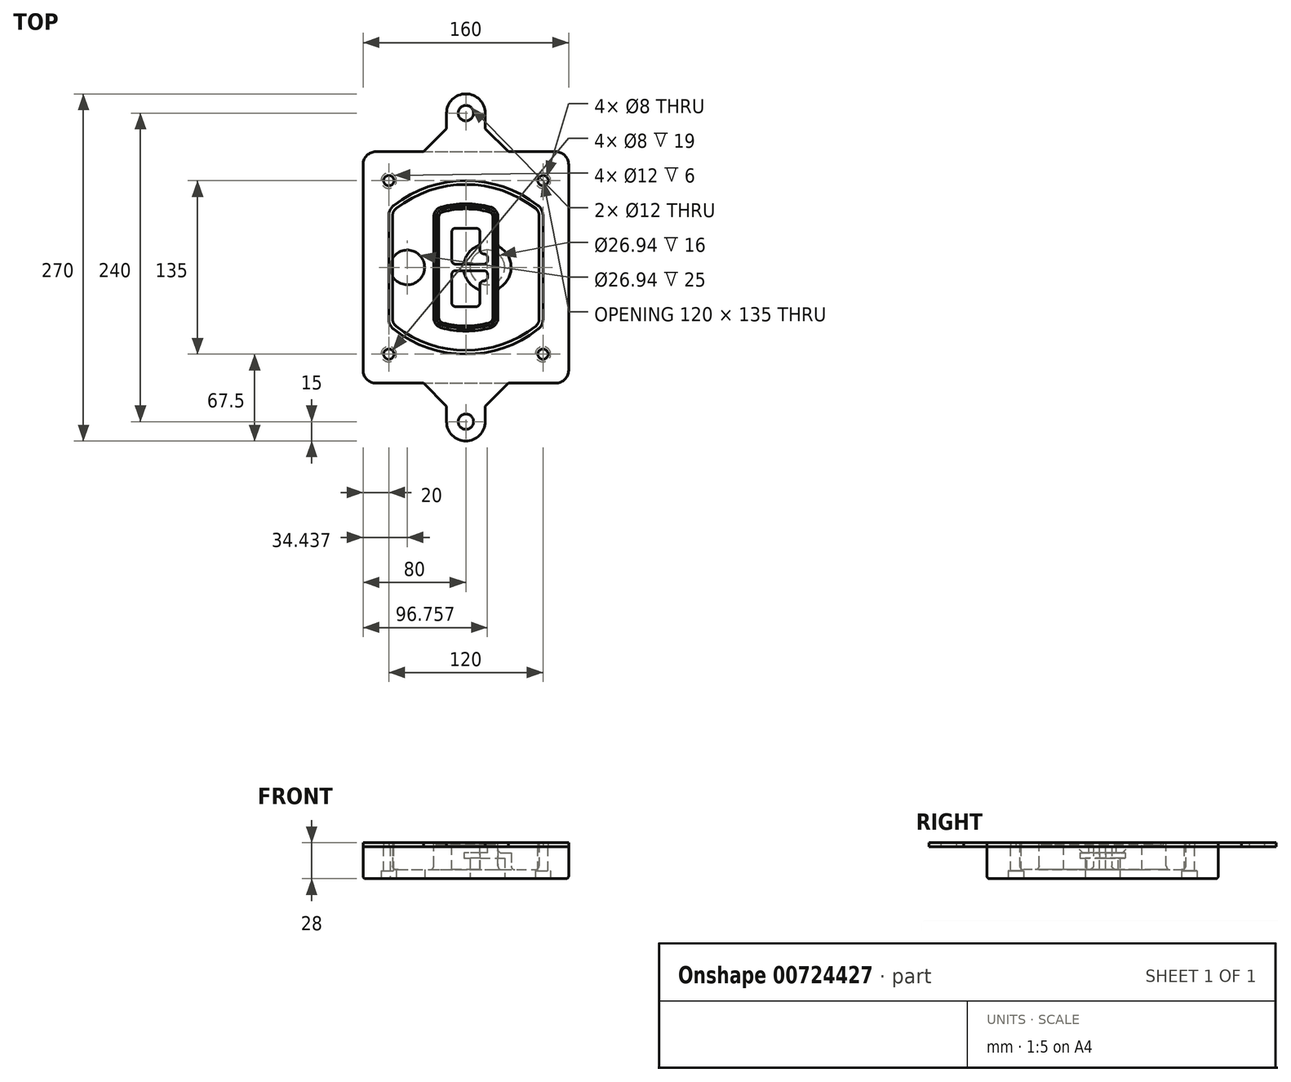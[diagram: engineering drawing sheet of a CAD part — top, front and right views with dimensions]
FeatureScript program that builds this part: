
annotation { "Feature Type Name" : "Feature", "Feature Type Description" : "" }
export const myFeature = defineFeature(function(context is Context, id is Id, definition is map)
    precondition{}
    {
        {
            var Q0;
            Q0=qCreatedBy(makeId("Top.planeOp"),FACE);
            var sketch = newSketch(context, id + "F0", { "sketchPlane" : qUnion([Q0])});
            skPoint(sketch, "E0.rect.middle", {"position": v(0, 0) * mm});
            skLineSegment(sketch, "E1.bottom", {"start": v(-70, -90) * mm, "end": v(70, -90) * mm});
            skLineSegment(sketch, "E1.top", {"start": v(-70, 90) * mm, "end": v(70, 90) * mm});
            skLineSegment(sketch, "E1.left", {"start": v(-80, -80) * mm, "end": v(-80, 80) * mm});
            skLineSegment(sketch, "E1.right", {"start": v(80, -80) * mm, "end": v(80, 80) * mm});
            skLineSegment(sketch, "E2", {"start": v(-80, 90) * mm, "end": v(80, -90) * mm, "construction": true});
            skLineSegment(sketch, "E3", {"start": v(80, 90) * mm, "end": v(-80, -90) * mm, "construction": true});
            skCircle(sketch, "E4", {"center": v(-60, 67.5) * mm, "radius": 4 * mm});
            skCircle(sketch, "E5", {"center": v(60, 67.5) * mm, "radius": 4 * mm});
            skCircle(sketch, "E6", {"center": v(60, -67.5) * mm, "radius": 4 * mm});
            skCircle(sketch, "E7", {"center": v(-60, -67.5) * mm, "radius": 4 * mm});
            skLineSegment(sketch, "E8", {"start": v(-60, 67.5) * mm, "end": v(60, 67.5) * mm, "construction": true});
            skLineSegment(sketch, "E9", {"start": v(60, 67.5) * mm, "end": v(60, -67.5) * mm, "construction": true});
            skLineSegment(sketch, "E10", {"start": v(60, -67.5) * mm, "end": v(-60, -67.5) * mm, "construction": true});
            skLineSegment(sketch, "E11", {"start": v(-60, -67.5) * mm, "end": v(-60, 67.5) * mm, "construction": true});
            skLineSegment(sketch, "E12", {"start": v(-60, 40.3) * mm, "end": v(-60, -40.3) * mm});
            skLineSegment(sketch, "E13", {"start": v(60, 40.3) * mm, "end": v(60, -40.3) * mm});
            skArc(sketch, "E14", {"start": v(56.15, 48.18) * mm, "mid": v(0, 67.5) * mm, "end": v(-56.15, 48.18) * mm});
            skArc(sketch, "E15", {"start": v(-56.15, -48.18) * mm, "mid": v(0, -67.5) * mm, "end": v(56.15, -48.18) * mm});
            skLineSegment(sketch, "E16", {"start": v(-60, 0) * mm, "end": v(60, 0) * mm, "construction": true});
            skPoint(sketch, "E17.visualSharp", {"position": v(-60, -45) * mm});
            skArc(sketch, "E17.filletArc", {"start": v(-60, -40.3) * mm, "mid": v(-58.99, -44.68) * mm, "end": v(-56.15, -48.18) * mm});
            skPoint(sketch, "E18.visualSharp", {"position": v(-60, 45) * mm});
            skArc(sketch, "E18.filletArc", {"start": v(-56.15, 48.18) * mm, "mid": v(-58.99, 44.68) * mm, "end": v(-60, 40.3) * mm});
            skPoint(sketch, "E19.visualSharp", {"position": v(60, 45) * mm});
            skArc(sketch, "E19.filletArc", {"start": v(60, 40.3) * mm, "mid": v(58.99, 44.68) * mm, "end": v(56.15, 48.18) * mm});
            skPoint(sketch, "E20.visualSharp", {"position": v(60, -45) * mm});
            skArc(sketch, "E20.filletArc", {"start": v(56.15, -48.18) * mm, "mid": v(58.99, -44.68) * mm, "end": v(60, -40.3) * mm});
            skPoint(sketch, "E21.visualSharp", {"position": v(-80, 90) * mm});
            skArc(sketch, "E21.filletArc", {"start": v(-70, 90) * mm, "mid": v(-77.07, 87.07) * mm, "end": v(-80, 80) * mm});
            skPoint(sketch, "E22.visualSharp", {"position": v(80, 90) * mm});
            skArc(sketch, "E22.filletArc", {"start": v(80, 80) * mm, "mid": v(77.07, 87.07) * mm, "end": v(70, 90) * mm});
            skPoint(sketch, "E23.visualSharp", {"position": v(80, -90) * mm});
            skArc(sketch, "E23.filletArc", {"start": v(70, -90) * mm, "mid": v(77.07, -87.07) * mm, "end": v(80, -80) * mm});
            skPoint(sketch, "E24.visualSharp", {"position": v(-80, -90) * mm});
            skArc(sketch, "E24.filletArc", {"start": v(-80, -80) * mm, "mid": v(-77.07, -87.07) * mm, "end": v(-70, -90) * mm});
            skArc(sketch, "E25.0", {"start": v(57, 40.3) * mm, "mid": v(56.3, 43.36) * mm, "end": v(54.3, 45.81) * mm});
            skLineSegment(sketch, "E25.1", {"start": v(57, 40.3) * mm, "end": v(57, -40.3) * mm});
            skArc(sketch, "E25.2", {"start": v(54.3, -45.81) * mm, "mid": v(56.3, -43.36) * mm, "end": v(57, -40.3) * mm});
            skArc(sketch, "E25.3", {"start": v(-54.3, -45.81) * mm, "mid": v(0, -64.5) * mm, "end": v(54.3, -45.81) * mm});
            skArc(sketch, "E25.4", {"start": v(-57, -40.3) * mm, "mid": v(-56.3, -43.36) * mm, "end": v(-54.3, -45.81) * mm});
            skArc(sketch, "E25.5", {"start": v(54.3, 45.81) * mm, "mid": v(0, 64.5) * mm, "end": v(-54.3, 45.81) * mm});
            skLineSegment(sketch, "E25.6", {"start": v(-57, 40.3) * mm, "end": v(-57, -40.3) * mm});
            skArc(sketch, "E25.7", {"start": v(-54.3, 45.81) * mm, "mid": v(-56.3, 43.36) * mm, "end": v(-57, 40.3) * mm});
            skArc(sketch, "E26.0", {"start": v(-58.62, 51.33) * mm, "mid": v(-62.58, 46.43) * mm, "end": v(-64, 40.3) * mm});
            skArc(sketch, "E26.1", {"start": v(58.62, 51.33) * mm, "mid": v(0, 71.5) * mm, "end": v(-58.62, 51.33) * mm});
            skArc(sketch, "E26.2", {"start": v(64, 40.3) * mm, "mid": v(62.58, 46.43) * mm, "end": v(58.62, 51.33) * mm});
            skLineSegment(sketch, "E26.3", {"start": v(64, 40.3) * mm, "end": v(64, -40.3) * mm});
            skArc(sketch, "E26.4", {"start": v(58.62, -51.33) * mm, "mid": v(62.58, -46.43) * mm, "end": v(64, -40.3) * mm});
            skLineSegment(sketch, "E26.5", {"start": v(-64, 40.3) * mm, "end": v(-64, -40.3) * mm});
            skArc(sketch, "E26.6", {"start": v(-58.62, -51.33) * mm, "mid": v(0, -71.5) * mm, "end": v(58.62, -51.33) * mm});
            skArc(sketch, "E26.7", {"start": v(-64, -40.3) * mm, "mid": v(-62.58, -46.43) * mm, "end": v(-58.62, -51.33) * mm});
            skSolve(sketch);
        }
        {
            var Q0;
            Q0=makeQuery(id+"F0.imprint","IMPRINT",FACE,{"disambiguationData":[TD([[makeQuery(id+"F0.imprint","IMPRINT",EDGE,{"derivedFrom":sQuery(id+"F0.wireOp",EDGE,"E1.bottom")}),1.0]])]});
            var Q1;
            Q1=makeQuery(id+"F0.imprint","IMPRINT",FACE,{"disambiguationData":[TD([[makeQuery(id+"F0.imprint","IMPRINT",EDGE,{"derivedFrom":sQuery(id+"F0.wireOp",EDGE,"E12")}),1.0]])]});
            var Q2;
            Q2=makeQuery(id+"F0.imprint","IMPRINT",FACE,{"disambiguationData":[TD([[makeQuery(id+"F0.imprint","IMPRINT",EDGE,{"derivedFrom":sQuery(id+"F0.wireOp",EDGE,"E25.0")}),1.0]])]});
            var Q3;
            Q3=makeQuery(id+"F0.imprint","IMPRINT",FACE,{"disambiguationData":[TD([[makeQuery(id+"F0.imprint","IMPRINT",EDGE,{"derivedFrom":sQuery(id+"F0.wireOp",EDGE,"E12")}),-1.0]])]});
            extrude(context, id + "F1", {"entities" : qUnion([Q0, Q1, Q2, Q3]), "oppositeDirection" : true, "depth" : 25 * mm});
        }
        {
            var Q0;
            Q0=makeQuery(id+"F0.imprint","IMPRINT",FACE,{"disambiguationData":[TD([[makeQuery(id+"F0.imprint","IMPRINT",EDGE,{"derivedFrom":sQuery(id+"F0.wireOp",EDGE,"E12")}),1.0]])]});
            extrude(context, id + "F2", {"entities" : qUnion([Q0]), "operationType" : NewBodyOperationType.ADD, "depth" : 3 * mm});
        }
        {
            var Q0;
            Q0=makeQuery(id+"F0.imprint","IMPRINT",FACE,{"disambiguationData":[TD([[makeQuery(id+"F0.imprint","IMPRINT",EDGE,{"derivedFrom":sQuery(id+"F0.wireOp",EDGE,"E25.0")}),1.0]])]});
            extrude(context, id + "F3", {"entities" : qUnion([Q0]), "operationType" : NewBodyOperationType.REMOVE, "oppositeDirection" : true, "depth" : 18 * mm});
        }
        {
            var Q0;
            Q0=makeQuery(id+"F2.opExtrude","CAP_FACE",FACE,{"disambiguationData":[OSD([sQuery(id+"F0.wireOp",EDGE,"E12"),sQuery(id+"F0.wireOp",EDGE,"E13"),sQuery(id+"F0.wireOp",EDGE,"E14"),sQuery(id+"F0.wireOp",EDGE,"E15"),sQuery(id+"F0.wireOp",EDGE,"E17.filletArc"),sQuery(id+"F0.wireOp",EDGE,"E18.filletArc"),sQuery(id+"F0.wireOp",EDGE,"E19.filletArc"),sQuery(id+"F0.wireOp",EDGE,"E20.filletArc"),sQuery(id+"F0.wireOp",EDGE,"E25.0"),sQuery(id+"F0.wireOp",EDGE,"E25.1"),sQuery(id+"F0.wireOp",EDGE,"E25.2"),sQuery(id+"F0.wireOp",EDGE,"E25.3"),sQuery(id+"F0.wireOp",EDGE,"E25.4"),sQuery(id+"F0.wireOp",EDGE,"E25.5"),sQuery(id+"F0.wireOp",EDGE,"E25.6"),sQuery(id+"F0.wireOp",EDGE,"E25.7")])],"isStart":false});
            var sketch = newSketch(context, id + "F4", { "sketchPlane" : qUnion([Q0])});
            skArc(sketch, "E27.0", {"start": v(-19.08, -46.97) * mm, "mid": v(0, -49.5) * mm, "end": v(19.08, -46.97) * mm});
            skArc(sketch, "E28.0", {"start": v(19.08, 46.97) * mm, "mid": v(0, 49.5) * mm, "end": v(-19.08, 46.97) * mm});
            skLineSegment(sketch, "E29", {"start": v(-25, 39.25) * mm, "end": v(-25, -39.25) * mm});
            skLineSegment(sketch, "E30", {"start": v(25, 39.25) * mm, "end": v(25, -39.25) * mm});
            skLineSegment(sketch, "E31", {"start": v(-25, 45.1) * mm, "end": v(25, 45.1) * mm, "construction": true});
            skLineSegment(sketch, "E32", {"start": v(-25, -45.1) * mm, "end": v(25, -45.1) * mm, "construction": true});
            skPoint(sketch, "E33.visualSharp", {"position": v(-25, 45.1) * mm});
            skArc(sketch, "E33.filletArc", {"start": v(-19.08, 46.97) * mm, "mid": v(-23.35, 44.11) * mm, "end": v(-25, 39.25) * mm});
            skPoint(sketch, "E34.visualSharp", {"position": v(25, 45.1) * mm});
            skArc(sketch, "E34.filletArc", {"start": v(25, 39.25) * mm, "mid": v(23.35, 44.11) * mm, "end": v(19.08, 46.97) * mm});
            skPoint(sketch, "E35.visualSharp", {"position": v(25, -45.1) * mm});
            skArc(sketch, "E35.filletArc", {"start": v(19.08, -46.97) * mm, "mid": v(23.35, -44.11) * mm, "end": v(25, -39.25) * mm});
            skPoint(sketch, "E36.visualSharp", {"position": v(-25, -45.1) * mm});
            skArc(sketch, "E36.filletArc", {"start": v(-25, -39.25) * mm, "mid": v(-23.35, -44.11) * mm, "end": v(-19.08, -46.97) * mm});
            skArc(sketch, "E37.0", {"start": v(54.3, 45.81) * mm, "mid": v(0, 64.5) * mm, "end": v(-54.3, 45.81) * mm});
            skArc(sketch, "E37.1", {"start": v(-54.3, 45.81) * mm, "mid": v(-56.3, 43.36) * mm, "end": v(-57, 40.3) * mm});
            skLineSegment(sketch, "E37.2", {"start": v(-57, 40.3) * mm, "end": v(-57, -40.3) * mm});
            skArc(sketch, "E37.3", {"start": v(-57, -40.3) * mm, "mid": v(-56.3, -43.36) * mm, "end": v(-54.3, -45.81) * mm});
            skArc(sketch, "E37.4", {"start": v(-54.3, -45.81) * mm, "mid": v(0, -64.5) * mm, "end": v(54.3, -45.81) * mm});
            skArc(sketch, "E37.5", {"start": v(54.3, -45.81) * mm, "mid": v(56.3, -43.36) * mm, "end": v(57, -40.3) * mm});
            skLineSegment(sketch, "E37.6", {"start": v(57, 40.3) * mm, "end": v(57, -40.3) * mm});
            skArc(sketch, "E37.7", {"start": v(57, 40.3) * mm, "mid": v(56.3, 43.36) * mm, "end": v(54.3, 45.81) * mm});
            skLineSegment(sketch, "E38.0", {"start": v(23, 39.25) * mm, "end": v(23, -39.25) * mm});
            skArc(sketch, "E38.1", {"start": v(18.56, -45.04) * mm, "mid": v(21.76, -42.9) * mm, "end": v(23, -39.25) * mm});
            skArc(sketch, "E38.2", {"start": v(-18.56, -45.04) * mm, "mid": v(0, -47.5) * mm, "end": v(18.56, -45.04) * mm});
            skArc(sketch, "E38.3", {"start": v(-23, -39.25) * mm, "mid": v(-21.76, -42.9) * mm, "end": v(-18.56, -45.04) * mm});
            skLineSegment(sketch, "E38.4", {"start": v(-23, 39.25) * mm, "end": v(-23, -39.25) * mm});
            skArc(sketch, "E38.5", {"start": v(23, 39.25) * mm, "mid": v(21.76, 42.9) * mm, "end": v(18.56, 45.04) * mm});
            skArc(sketch, "E38.6", {"start": v(-18.56, 45.04) * mm, "mid": v(-21.76, 42.9) * mm, "end": v(-23, 39.25) * mm});
            skArc(sketch, "E38.7", {"start": v(18.56, 45.04) * mm, "mid": v(0, 47.5) * mm, "end": v(-18.56, 45.04) * mm});
            skArc(sketch, "E39.0", {"start": v(21, 39.25) * mm, "mid": v(20.18, 41.68) * mm, "end": v(18.04, 43.1) * mm});
            skLineSegment(sketch, "E39.1", {"start": v(21, 39.25) * mm, "end": v(21, -39.25) * mm});
            skArc(sketch, "E39.2", {"start": v(18.04, -43.1) * mm, "mid": v(20.18, -41.68) * mm, "end": v(21, -39.25) * mm});
            skArc(sketch, "E39.3", {"start": v(-18.04, -43.1) * mm, "mid": v(0, -45.5) * mm, "end": v(18.04, -43.1) * mm});
            skArc(sketch, "E39.4", {"start": v(-21, -39.25) * mm, "mid": v(-20.18, -41.68) * mm, "end": v(-18.04, -43.1) * mm});
            skArc(sketch, "E39.5", {"start": v(18.04, 43.1) * mm, "mid": v(0, 45.5) * mm, "end": v(-18.04, 43.1) * mm});
            skLineSegment(sketch, "E39.6", {"start": v(-21, 39.25) * mm, "end": v(-21, -39.25) * mm});
            skArc(sketch, "E39.7", {"start": v(-18.04, 43.1) * mm, "mid": v(-20.18, 41.68) * mm, "end": v(-21, 39.25) * mm});
            skLineSegment(sketch, "E40", {"start": v(-25, 0) * mm, "end": v(25, 0) * mm, "construction": true});
            skLineSegment(sketch, "E41", {"start": v(-11, 5.5) * mm, "end": v(-11, 27.5) * mm});
            skLineSegment(sketch, "E42", {"start": v(-8, 30.5) * mm, "end": v(8, 30.5) * mm});
            skLineSegment(sketch, "E43", {"start": v(11, 27.5) * mm, "end": v(11, 13.5) * mm});
            skLineSegment(sketch, "E44", {"start": v(14, 10.5) * mm, "end": v(14, 10.5) * mm});
            skLineSegment(sketch, "E45", {"start": v(17, 7.5) * mm, "end": v(17, 5.5) * mm});
            skLineSegment(sketch, "E46", {"start": v(14, 2.5) * mm, "end": v(-8, 2.5) * mm});
            skPoint(sketch, "E47.visualSharp", {"position": v(-11, 30.5) * mm});
            skArc(sketch, "E47.filletArc", {"start": v(-8, 30.5) * mm, "mid": v(-10.12, 29.62) * mm, "end": v(-11, 27.5) * mm});
            skPoint(sketch, "E48.visualSharp", {"position": v(11, 30.5) * mm});
            skArc(sketch, "E48.filletArc", {"start": v(11, 27.5) * mm, "mid": v(10.12, 29.62) * mm, "end": v(8, 30.5) * mm});
            skPoint(sketch, "E49.visualSharp", {"position": v(11, 10.5) * mm});
            skArc(sketch, "E49.filletArc", {"start": v(11, 13.5) * mm, "mid": v(11.88, 11.38) * mm, "end": v(14, 10.5) * mm});
            skPoint(sketch, "E50.visualSharp", {"position": v(17, 10.5) * mm});
            skArc(sketch, "E50.filletArc", {"start": v(17, 7.5) * mm, "mid": v(16.12, 9.62) * mm, "end": v(14, 10.5) * mm});
            skPoint(sketch, "E51.visualSharp", {"position": v(17, 2.5) * mm});
            skArc(sketch, "E51.filletArc", {"start": v(14, 2.5) * mm, "mid": v(16.12, 3.38) * mm, "end": v(17, 5.5) * mm});
            skPoint(sketch, "E52.visualSharp", {"position": v(-11, 2.5) * mm});
            skArc(sketch, "E52.filletArc", {"start": v(-11, 5.5) * mm, "mid": v(-10.12, 3.38) * mm, "end": v(-8, 2.5) * mm});
            skLineSegment(sketch, "E53.0.MirrorCS", {"start": v(14, -2.5) * mm, "end": v(-8, -2.5) * mm});
            skArc(sketch, "E54.0.MirrorCS", {"start": v(-11, -5.5) * mm, "mid": v(-10.12, -3.38) * mm, "end": v(-8, -2.5) * mm});
            skLineSegment(sketch, "E55.0.MirrorCS", {"start": v(-11, -5.5) * mm, "end": v(-11, -27.5) * mm});
            skArc(sketch, "E56.0.MirrorCS", {"start": v(-8, -30.5) * mm, "mid": v(-10.12, -29.62) * mm, "end": v(-11, -27.5) * mm});
            skLineSegment(sketch, "E57.0.MirrorCS", {"start": v(-8, -30.5) * mm, "end": v(8, -30.5) * mm});
            skArc(sketch, "E58.0.MirrorCS", {"start": v(11, -27.5) * mm, "mid": v(10.12, -29.62) * mm, "end": v(8, -30.5) * mm});
            skLineSegment(sketch, "E59.0.MirrorCS", {"start": v(11, -27.5) * mm, "end": v(11, -13.5) * mm});
            skArc(sketch, "E60.0.MirrorCS", {"start": v(11, -13.5) * mm, "mid": v(11.88, -11.38) * mm, "end": v(14, -10.5) * mm});
            skArc(sketch, "E61.0.MirrorCS", {"start": v(17, -7.5) * mm, "mid": v(16.12, -9.62) * mm, "end": v(14, -10.5) * mm});
            skLineSegment(sketch, "E62.0.MirrorCS", {"start": v(17, -7.5) * mm, "end": v(17, -5.5) * mm});
            skArc(sketch, "E63.0.MirrorCS", {"start": v(14, -2.5) * mm, "mid": v(16.12, -3.38) * mm, "end": v(17, -5.5) * mm});
            skSolve(sketch);
        }
        {
            var Q0;
            Q0=makeQuery(id+"F4.imprint","IMPRINT",FACE,{"disambiguationData":[TD([[makeQuery(id+"F4.imprint","IMPRINT",EDGE,{"derivedFrom":sQuery(id+"F4.wireOp",EDGE,"E27.0")}),1.0]])]});
            var Q1;
            Q1=makeQuery(id+"F4.imprint","IMPRINT",FACE,{"disambiguationData":[TD([[makeQuery(id+"F4.imprint","IMPRINT",EDGE,{"derivedFrom":sQuery(id+"F4.wireOp",EDGE,"E38.0")}),-1.0]])]});
            var Q2;
            Q2=makeQuery(id+"F4.imprint","IMPRINT",FACE,{"disambiguationData":[TD([[makeQuery(id+"F4.imprint","IMPRINT",EDGE,{"derivedFrom":sQuery(id+"F4.wireOp",EDGE,"E39.0")}),1.0]])]});
            extrude(context, id + "F5", {"entities" : qUnion([Q0, Q1, Q2]), "operationType" : NewBodyOperationType.ADD, "endBound" : BoundingType.UP_TO_NEXT, "oppositeDirection" : true, "depth" : 25 * mm});
        }
        {
            var Q0;
            Q0=makeQuery(id+"F4.imprint","IMPRINT",FACE,{"disambiguationData":[TD([[makeQuery(id+"F4.imprint","IMPRINT",EDGE,{"derivedFrom":sQuery(id+"F4.wireOp",EDGE,"E38.0")}),-1.0]])]});
            extrude(context, id + "F6", {"entities" : qUnion([Q0]), "operationType" : NewBodyOperationType.REMOVE, "oppositeDirection" : true, "depth" : 2 * mm});
        }
        {
            var Q0;
            Q0=makeQuery(id+"F1.opExtrude","CAP_FACE",FACE,{"disambiguationData":[OSD([sQuery(id+"F0.wireOp",EDGE,"E1.bottom"),sQuery(id+"F0.wireOp",EDGE,"E1.top"),sQuery(id+"F0.wireOp",EDGE,"E1.left"),sQuery(id+"F0.wireOp",EDGE,"E1.right"),sQuery(id+"F0.wireOp",EDGE,"E4"),sQuery(id+"F0.wireOp",EDGE,"E5"),sQuery(id+"F0.wireOp",EDGE,"E6"),sQuery(id+"F0.wireOp",EDGE,"E7"),sQuery(id+"F0.wireOp",EDGE,"E21.filletArc"),sQuery(id+"F0.wireOp",EDGE,"E22.filletArc"),sQuery(id+"F0.wireOp",EDGE,"E23.filletArc"),sQuery(id+"F0.wireOp",EDGE,"E24.filletArc")])],"isStart":false});
            var sketch = newSketch(context, id + "F7", { "sketchPlane" : qUnion([Q0])});
            skCircle(sketch, "E64", {"center": v(16.76, 0) * mm, "radius": 13.47 * mm});
            skCircle(sketch, "E65", {"center": v(-45.56, 0) * mm, "radius": 13.47 * mm});
            skLineSegment(sketch, "E66", {"start": v(80, 0) * mm, "end": v(-80, 0) * mm});
            skCircle(sketch, "E67", {"center": v(16.76, 0) * mm, "radius": 18.47 * mm});
            skCircle(sketch, "E68", {"center": v(60, -67.5) * mm, "radius": 6 * mm});
            skCircle(sketch, "E69", {"center": v(-60, -67.5) * mm, "radius": 6 * mm});
            skCircle(sketch, "E70", {"center": v(-60, 67.5) * mm, "radius": 6 * mm});
            skCircle(sketch, "E71", {"center": v(60, 67.5) * mm, "radius": 6 * mm});
            skSolve(sketch);
        }
        {
            var Q0;
            {var subQ1=sQuery(id+"F7.wireOp",EDGE,"E66");var subQ4=sQuery(id+"F7.wireOp",EDGE,"E64");var subQ6=makeQuery(id+"F7.imprint","INTERSECT",VERTEX,{"disambiguationData":[OD(0.0)],"derivedFrom":[subQ4,subQ1]});Q0=makeQuery(id+"F7.imprint","IMPRINT",FACE,{"disambiguationData":[TD([[makeQuery(id+"F7.imprint","IMPRINT",EDGE,{"disambiguationData":[TD([[subQ6,-1.0]])],"derivedFrom":subQ4}),-1.0]])]});}
            var Q1;
            {var subQ0=sQuery(id+"F7.wireOp",EDGE,"E66");var subQ1=sQuery(id+"F7.wireOp",EDGE,"E64");var subQ3=makeQuery(id+"F7.imprint","INTERSECT",VERTEX,{"disambiguationData":[OD(0.0)],"derivedFrom":[subQ1,subQ0]});Q1=makeQuery(id+"F7.imprint","IMPRINT",FACE,{"disambiguationData":[TD([[makeQuery(id+"F7.imprint","IMPRINT",EDGE,{"disambiguationData":[TD([[subQ3,-1.0]])],"derivedFrom":subQ1}),1.0]])]});}
            var Q2;
            {var subQ0=sQuery(id+"F7.wireOp",EDGE,"E66");var subQ1=sQuery(id+"F7.wireOp",EDGE,"E64");var subQ3=makeQuery(id+"F7.imprint","INTERSECT",VERTEX,{"disambiguationData":[OD(0.0)],"derivedFrom":[subQ1,subQ0]});Q2=makeQuery(id+"F7.imprint","IMPRINT",FACE,{"disambiguationData":[TD([[makeQuery(id+"F7.imprint","IMPRINT",EDGE,{"disambiguationData":[TD([[subQ3,1.0]])],"derivedFrom":subQ1}),1.0]])]});}
            var Q3;
            {var subQ1=sQuery(id+"F7.wireOp",EDGE,"E66");var subQ4=sQuery(id+"F7.wireOp",EDGE,"E64");var subQ6=makeQuery(id+"F7.imprint","INTERSECT",VERTEX,{"disambiguationData":[OD(0.0)],"derivedFrom":[subQ4,subQ1]});Q3=makeQuery(id+"F7.imprint","IMPRINT",FACE,{"disambiguationData":[TD([[makeQuery(id+"F7.imprint","IMPRINT",EDGE,{"disambiguationData":[TD([[subQ6,1.0]])],"derivedFrom":subQ4}),-1.0]])]});}
            extrude(context, id + "F8", {"entities" : qUnion([Q0, Q1, Q2, Q3]), "operationType" : NewBodyOperationType.ADD, "oppositeDirection" : true, "depth" : 20 * mm});
        }
        {
            var Q0;
            {var subQ0=sQuery(id+"F7.wireOp",EDGE,"E66");var subQ1=sQuery(id+"F7.wireOp",EDGE,"E64");var subQ3=makeQuery(id+"F7.imprint","INTERSECT",VERTEX,{"disambiguationData":[OD(0.0)],"derivedFrom":[subQ1,subQ0]});Q0=makeQuery(id+"F7.imprint","IMPRINT",FACE,{"disambiguationData":[TD([[makeQuery(id+"F7.imprint","IMPRINT",EDGE,{"disambiguationData":[TD([[subQ3,-1.0]])],"derivedFrom":subQ1}),1.0]])]});}
            var Q1;
            {var subQ0=sQuery(id+"F7.wireOp",EDGE,"E66");var subQ1=sQuery(id+"F7.wireOp",EDGE,"E64");var subQ3=makeQuery(id+"F7.imprint","INTERSECT",VERTEX,{"disambiguationData":[OD(0.0)],"derivedFrom":[subQ1,subQ0]});Q1=makeQuery(id+"F7.imprint","IMPRINT",FACE,{"disambiguationData":[TD([[makeQuery(id+"F7.imprint","IMPRINT",EDGE,{"disambiguationData":[TD([[subQ3,1.0]])],"derivedFrom":subQ1}),1.0]])]});}
            extrude(context, id + "F9", {"entities" : qUnion([Q0, Q1]), "operationType" : NewBodyOperationType.REMOVE, "oppositeDirection" : true, "depth" : 16 * mm});
        }
        {
            var Q0;
            {var subQ0=sQuery(id+"F7.wireOp",EDGE,"E66");var subQ1=sQuery(id+"F7.wireOp",EDGE,"E65");var subQ3=makeQuery(id+"F7.imprint","INTERSECT",VERTEX,{"disambiguationData":[OD(0.0)],"derivedFrom":[subQ1,subQ0]});Q0=makeQuery(id+"F7.imprint","IMPRINT",FACE,{"disambiguationData":[TD([[makeQuery(id+"F7.imprint","IMPRINT",EDGE,{"disambiguationData":[TD([[subQ3,-1.0]])],"derivedFrom":subQ1}),1.0]])]});}
            var Q1;
            {var subQ0=sQuery(id+"F7.wireOp",EDGE,"E66");var subQ1=sQuery(id+"F7.wireOp",EDGE,"E65");var subQ3=makeQuery(id+"F7.imprint","INTERSECT",VERTEX,{"disambiguationData":[OD(0.0)],"derivedFrom":[subQ1,subQ0]});Q1=makeQuery(id+"F7.imprint","IMPRINT",FACE,{"disambiguationData":[TD([[makeQuery(id+"F7.imprint","IMPRINT",EDGE,{"disambiguationData":[TD([[subQ3,1.0]])],"derivedFrom":subQ1}),1.0]])]});}
            extrude(context, id + "F10", {"entities" : qUnion([Q0, Q1]), "operationType" : NewBodyOperationType.REMOVE, "oppositeDirection" : true, "depth" : 25 * mm});
        }
        {
            var Q0;
            Q0=makeQuery(id+"F7.imprint","IMPRINT",FACE,{"disambiguationData":[TD([[makeQuery(id+"F7.imprint","IMPRINT",EDGE,{"derivedFrom":sQuery(id+"F7.wireOp",EDGE,"E68")}),1.0]])]});
            var Q1;
            Q1=makeQuery(id+"F7.imprint","IMPRINT",FACE,{"disambiguationData":[TD([[makeQuery(id+"F7.imprint","IMPRINT",EDGE,{"derivedFrom":makeQuery(id+"F1.opExtrude","CAP_EDGE",EDGE,{"disambiguationData":[OSD([sQuery(id+"F0.wireOp",EDGE,"E5")])],"isStart":false})}),-1.0]])]});
            var Q2;
            Q2=makeQuery(id+"F7.imprint","IMPRINT",FACE,{"disambiguationData":[TD([[makeQuery(id+"F7.imprint","IMPRINT",EDGE,{"derivedFrom":sQuery(id+"F7.wireOp",EDGE,"E69")}),1.0]])]});
            var Q3;
            Q3=makeQuery(id+"F7.imprint","IMPRINT",FACE,{"disambiguationData":[TD([[makeQuery(id+"F7.imprint","IMPRINT",EDGE,{"derivedFrom":makeQuery(id+"F1.opExtrude","CAP_EDGE",EDGE,{"disambiguationData":[OSD([sQuery(id+"F0.wireOp",EDGE,"E4")])],"isStart":false})}),-1.0]])]});
            var Q4;
            Q4=makeQuery(id+"F7.imprint","IMPRINT",FACE,{"disambiguationData":[TD([[makeQuery(id+"F7.imprint","IMPRINT",EDGE,{"derivedFrom":sQuery(id+"F7.wireOp",EDGE,"E70")}),1.0]])]});
            var Q5;
            Q5=makeQuery(id+"F7.imprint","IMPRINT",FACE,{"disambiguationData":[TD([[makeQuery(id+"F7.imprint","IMPRINT",EDGE,{"derivedFrom":makeQuery(id+"F1.opExtrude","CAP_EDGE",EDGE,{"disambiguationData":[OSD([sQuery(id+"F0.wireOp",EDGE,"E7")])],"isStart":false})}),-1.0]])]});
            var Q6;
            Q6=makeQuery(id+"F7.imprint","IMPRINT",FACE,{"disambiguationData":[TD([[makeQuery(id+"F7.imprint","IMPRINT",EDGE,{"derivedFrom":sQuery(id+"F7.wireOp",EDGE,"E71")}),1.0]])]});
            var Q7;
            Q7=makeQuery(id+"F7.imprint","IMPRINT",FACE,{"disambiguationData":[TD([[makeQuery(id+"F7.imprint","IMPRINT",EDGE,{"derivedFrom":makeQuery(id+"F1.opExtrude","CAP_EDGE",EDGE,{"disambiguationData":[OSD([sQuery(id+"F0.wireOp",EDGE,"E6")])],"isStart":false})}),-1.0]])]});
            extrude(context, id + "F11", {"entities" : qUnion([Q0, Q1, Q2, Q3, Q4, Q5, Q6, Q7]), "operationType" : NewBodyOperationType.REMOVE, "oppositeDirection" : true, "depth" : 6 * mm});
        }
        {
            var Q0;
            Q0=makeQuery(id+"F9.boolean.opBoolean","COPY",FACE,{"derivedFrom":makeQuery(id+"F9.opExtrude","CAP_FACE",FACE,{"disambiguationData":[OSD([sQuery(id+"F7.wireOp",EDGE,"E64")])],"isStart":false})});
            var sketch = newSketch(context, id + "F12", { "sketchPlane" : qUnion([Q0])});
            skArc(sketch, "E72.0", {"start": v(11, 17.55) * mm, "mid": v(2.57, 11.82) * mm, "end": v(-1.54, 2.5) * mm});
            skArc(sketch, "E72.1", {"start": v(-1.54, -2.5) * mm, "mid": v(2.57, -11.82) * mm, "end": v(11, -17.55) * mm});
            skLineSegment(sketch, "E73", {"start": v(-1.54, -2.5) * mm, "end": v(14, -2.5) * mm});
            skLineSegment(sketch, "E74.0", {"start": v(14, 2.5) * mm, "end": v(-1.54, 2.5) * mm});
            skArc(sketch, "E74.1", {"start": v(14, 2.5) * mm, "mid": v(16.12, 3.38) * mm, "end": v(17, 5.5) * mm});
            skLineSegment(sketch, "E74.2", {"start": v(17, 7.5) * mm, "end": v(17, 5.5) * mm});
            skArc(sketch, "E74.3", {"start": v(17, 7.5) * mm, "mid": v(16.12, 9.62) * mm, "end": v(14, 10.5) * mm});
            skArc(sketch, "E74.4", {"start": v(11, 13.5) * mm, "mid": v(11.88, 11.38) * mm, "end": v(14, 10.5) * mm});
            skLineSegment(sketch, "E74.5", {"start": v(11, 17.55) * mm, "end": v(11, 13.5) * mm});
            skLineSegment(sketch, "E74.7", {"start": v(14, -2.5) * mm, "end": v(-1.54, -2.5) * mm});
            skArc(sketch, "E74.8", {"start": v(14, -2.5) * mm, "mid": v(16.12, -3.38) * mm, "end": v(17, -5.5) * mm});
            skLineSegment(sketch, "E74.9", {"start": v(17, -7.5) * mm, "end": v(17, -5.5) * mm});
            skArc(sketch, "E74.10", {"start": v(17, -7.5) * mm, "mid": v(16.12, -9.62) * mm, "end": v(14, -10.5) * mm});
            skArc(sketch, "E74.11", {"start": v(11, -13.5) * mm, "mid": v(11.88, -11.38) * mm, "end": v(14, -10.5) * mm});
            skLineSegment(sketch, "E74.12", {"start": v(11, -17.55) * mm, "end": v(11, -13.5) * mm});
            skPoint(sketch, "E75.orphan", {"position": v(11, -27.5) * mm});
            skPoint(sketch, "E76.orphan", {"position": v(-8, -2.5) * mm});
            skPoint(sketch, "E77.orphan", {"position": v(-8, 2.5) * mm});
            skPoint(sketch, "E78.orphan", {"position": v(11, 27.5) * mm});
            skSolve(sketch);
        }
        {
            var Q0;
            {var subQ7=sQuery(id+"F12.wireOp",EDGE,"E72.0");var subQ14=sQuery(id+"F12.wireOp",EDGE,"E72.1");var subQ16=sQuery(id+"F12.wireOp",EDGE,"E74.1");var subQ18=sQuery(id+"F12.wireOp",EDGE,"E74.8");Q0=qUnion([makeQuery(id+"F12.imprint","IMPRINT",FACE,{"disambiguationData":[TD([[makeQuery(id+"F12.imprint","IMPRINT",EDGE,{"derivedFrom":subQ7}),1.0]])]}),makeQuery(id+"F12.imprint","IMPRINT",FACE,{"disambiguationData":[TD([[makeQuery(id+"F12.imprint","IMPRINT",EDGE,{"derivedFrom":subQ14}),1.0]])]}),makeQuery(id+"F12.imprint","IMPRINT",FACE,{"disambiguationData":[TD([[makeQuery(id+"F12.imprint","IMPRINT",EDGE,{"derivedFrom":subQ16}),1.0]])]}),makeQuery(id+"F12.imprint","IMPRINT",FACE,{"disambiguationData":[TD([[makeQuery(id+"F12.imprint","IMPRINT",EDGE,{"derivedFrom":subQ18}),-1.0]])]})]);}
            var Q1;
            Q1=makeQuery(id+"F5.boolean.opBoolean","SPLIT",FACE,{"disambiguationData":[TD([makeQuery(id+"F5.opExtrude","SWEPT_FACE",FACE,{"disambiguationData":[OSD([sQuery(id+"F4.wireOp",EDGE,"E41")])]})])],"derivedFrom":makeQuery(id+"F3.boolean.opBoolean","COPY",FACE,{"derivedFrom":makeQuery(id+"F3.opExtrude","CAP_FACE",FACE,{"disambiguationData":[OSD([sQuery(id+"F0.wireOp",EDGE,"E25.0"),sQuery(id+"F0.wireOp",EDGE,"E25.1"),sQuery(id+"F0.wireOp",EDGE,"E25.2"),sQuery(id+"F0.wireOp",EDGE,"E25.3"),sQuery(id+"F0.wireOp",EDGE,"E25.4"),sQuery(id+"F0.wireOp",EDGE,"E25.5"),sQuery(id+"F0.wireOp",EDGE,"E25.6"),sQuery(id+"F0.wireOp",EDGE,"E25.7")])],"isStart":false})})});
            extrude(context, id + "F13", {"entities" : qUnion([Q0]), "operationType" : NewBodyOperationType.REMOVE, "endBound" : BoundingType.UP_TO_SURFACE, "endBoundEntityFace" : qUnion([Q1]), "depth" : 25 * mm});
        }
        {
            var Q0;
            Q0=makeQuery(id+"F3.boolean.opBoolean","COPY",EDGE,{"derivedFrom":makeQuery(id+"F3.opExtrude","CAP_EDGE",EDGE,{"disambiguationData":[OSD([sQuery(id+"F0.wireOp",EDGE,"E25.6")])],"isStart":false})});
            var Q1;
            Q1=makeQuery(id+"F8.boolean.opBoolean","INTERSECT",EDGE,{"derivedFrom":[makeQuery(id+"F5.opExtrude","SWEPT_FACE",FACE,{"disambiguationData":[OSD([sQuery(id+"F4.wireOp",EDGE,"E30")])]}),makeQuery(id+"F8.opExtrude","CAP_FACE",FACE,{"disambiguationData":[OSD([sQuery(id+"F7.wireOp",EDGE,"E67")])],"isStart":false})]});
            var Q2;
            Q2=makeQuery(id+"F8.boolean.opBoolean","INTERSECT",EDGE,{"disambiguationData":[OD(1.0)],"derivedFrom":[makeQuery(id+"F5.opExtrude","SWEPT_FACE",FACE,{"disambiguationData":[OSD([sQuery(id+"F4.wireOp",EDGE,"E30")])]}),makeQuery(id+"F8.opExtrude","SWEPT_FACE",FACE,{"disambiguationData":[OSD([sQuery(id+"F7.wireOp",EDGE,"E67")])]})]});
            var Q3;
            {var subQ0=sQuery(id+"F4.wireOp",EDGE,"E30");Q3=makeQuery(id+"F8.boolean.opBoolean","SPLIT",EDGE,{"disambiguationData":[TD([makeQuery(id+"F5.opExtrude","SWEPT_FACE",FACE,{"disambiguationData":[OSD([sQuery(id+"F4.wireOp",EDGE,"E35.filletArc")])]})])],"derivedFrom":makeQuery(id+"F5.opExtrude","CAP_EDGE",EDGE,{"disambiguationData":[OSD([subQ0])],"isStart":false})});}
            var Q4;
            {var subQ0=sQuery(id+"F0.wireOp",EDGE,"E25.7");var subQ1=sQuery(id+"F0.wireOp",EDGE,"E25.1");var subQ2=sQuery(id+"F0.wireOp",EDGE,"E25.6");var subQ3=sQuery(id+"F0.wireOp",EDGE,"E25.5");var subQ4=sQuery(id+"F0.wireOp",EDGE,"E25.4");var subQ5=sQuery(id+"F0.wireOp",EDGE,"E25.0");var subQ6=sQuery(id+"F0.wireOp",EDGE,"E25.2");var subQ7=sQuery(id+"F0.wireOp",EDGE,"E25.3");Q4=makeQuery(id+"F8.boolean.opBoolean","INTERSECT",EDGE,{"derivedFrom":[makeQuery(id+"F5.boolean.opBoolean","SPLIT",FACE,{"disambiguationData":[TD([makeQuery(id+"F2.opExtrude","SWEPT_FACE",FACE,{"disambiguationData":[OSD([subQ5])]})])],"derivedFrom":makeQuery(id+"F3.boolean.opBoolean","COPY",FACE,{"derivedFrom":makeQuery(id+"F3.opExtrude","CAP_FACE",FACE,{"disambiguationData":[OSD([subQ5,subQ1,subQ6,subQ7,subQ4,subQ3,subQ2,subQ0])],"isStart":false})})}),makeQuery(id+"F8.opExtrude","SWEPT_FACE",FACE,{"disambiguationData":[OSD([sQuery(id+"F7.wireOp",EDGE,"E67")])]})]});}
            var Q5;
            Q5=makeQuery(id+"F8.boolean.opBoolean","INTERSECT",EDGE,{"disambiguationData":[OD(0.0)],"derivedFrom":[makeQuery(id+"F5.opExtrude","SWEPT_FACE",FACE,{"disambiguationData":[OSD([sQuery(id+"F4.wireOp",EDGE,"E30")])]}),makeQuery(id+"F8.opExtrude","SWEPT_FACE",FACE,{"disambiguationData":[OSD([sQuery(id+"F7.wireOp",EDGE,"E67")])]})]});
            fillet(context, id + "F14", {"entities" : qUnion([Q0, Q1, Q2, Q3, Q4, Q5]), "radius" : 3 * mm, "tangentPropagation" : true, "allowEdgeOverflow" : false});
        }
        {
            var Q0;
            Q0=makeQuery(id+"F1.opExtrude","CAP_EDGE",EDGE,{"disambiguationData":[OSD([sQuery(id+"F0.wireOp",EDGE,"E1.bottom")])],"isStart":false});
            fillet(context, id + "F15", {"entities" : qUnion([Q0]), "radius" : 2 * mm, "tangentPropagation" : true, "allowEdgeOverflow" : false});
        }
        {
            var Q0;
            {var subQ0=sQuery(id+"F0.wireOp",EDGE,"E21.filletArc");var subQ1=sQuery(id+"F0.wireOp",EDGE,"E7");var subQ2=sQuery(id+"F0.wireOp",EDGE,"E6");var subQ3=sQuery(id+"F0.wireOp",EDGE,"E5");var subQ4=sQuery(id+"F0.wireOp",EDGE,"E4");var subQ5=sQuery(id+"F0.wireOp",EDGE,"E22.filletArc");var subQ6=sQuery(id+"F0.wireOp",EDGE,"E1.bottom");var subQ7=sQuery(id+"F0.wireOp",EDGE,"E1.right");var subQ8=sQuery(id+"F0.wireOp",EDGE,"E1.top");var subQ9=sQuery(id+"F0.wireOp",EDGE,"E1.left");var subQ10=sQuery(id+"F0.wireOp",EDGE,"E23.filletArc");var subQ11=sQuery(id+"F0.wireOp",EDGE,"E24.filletArc");Q0=makeQuery(id+"F2.boolean.opBoolean","SPLIT",FACE,{"disambiguationData":[TD([makeQuery(id+"F1.opExtrude","SWEPT_FACE",FACE,{"disambiguationData":[OSD([subQ6])]})])],"derivedFrom":makeQuery(id+"F1.opExtrude","CAP_FACE",FACE,{"disambiguationData":[OSD([subQ6,subQ8,subQ9,subQ7,subQ4,subQ3,subQ2,subQ1,subQ0,subQ5,subQ10,subQ11])],"isStart":true})});}
            var sketch = newSketch(context, id + "F16", { "sketchPlane" : qUnion([Q0])});
            skLineSegment(sketch, "E79.0", {"start": v(-80, -80) * mm, "end": v(-80, 80) * mm});
            skLineSegment(sketch, "E80.0", {"start": v(-70, -90) * mm, "end": v(70, -90) * mm});
            skLineSegment(sketch, "E81.0", {"start": v(80, -80) * mm, "end": v(80, 80) * mm});
            skCircle(sketch, "E82.0", {"center": v(60, 67.5) * mm, "radius": 4 * mm});
            skCircle(sketch, "E83.0", {"center": v(-60, 67.5) * mm, "radius": 4 * mm});
            skCircle(sketch, "E84.0", {"center": v(-60, -67.5) * mm, "radius": 4 * mm});
            skCircle(sketch, "E85.0", {"center": v(60, -67.5) * mm, "radius": 4 * mm});
            skArc(sketch, "E86.0", {"start": v(56.15, 48.18) * mm, "mid": v(0, 67.5) * mm, "end": v(-56.15, 48.18) * mm});
            skArc(sketch, "E87.0", {"start": v(54.3, 45.81) * mm, "mid": v(0, 64.5) * mm, "end": v(-54.3, 45.81) * mm});
            skLineSegment(sketch, "E88.0", {"start": v(-60, 40.3) * mm, "end": v(-60, -40.3) * mm});
            skLineSegment(sketch, "E89.0", {"start": v(-57, 40.3) * mm, "end": v(-57, -40.3) * mm});
            skArc(sketch, "E90.0", {"start": v(-54.3, -45.81) * mm, "mid": v(0, -64.5) * mm, "end": v(54.3, -45.81) * mm});
            skArc(sketch, "E91.0", {"start": v(-56.15, -48.18) * mm, "mid": v(0, -67.5) * mm, "end": v(56.15, -48.18) * mm});
            skLineSegment(sketch, "E92.0", {"start": v(60, 40.3) * mm, "end": v(60, -40.3) * mm});
            skLineSegment(sketch, "E93.0", {"start": v(57, 40.3) * mm, "end": v(57, -40.3) * mm});
            skLineSegment(sketch, "E94.0", {"start": v(-70, 90) * mm, "end": v(70, 90) * mm});
            skLineSegment(sketch, "E95", {"start": v(0, 90) * mm, "end": v(0, 120) * mm, "construction": true});
            skCircle(sketch, "E96", {"center": v(0, 120) * mm, "radius": 6 * mm});
            skLineSegment(sketch, "E97", {"start": v(-33, 90) * mm, "end": v(-15, 108) * mm});
            skLineSegment(sketch, "E98", {"start": v(-15, 108) * mm, "end": v(-15, 120) * mm});
            skArc(sketch, "E99", {"start": v(-15, 120) * mm, "mid": v(0, 135) * mm, "end": v(15, 120) * mm});
            skLineSegment(sketch, "E100", {"start": v(15, 120) * mm, "end": v(15, 108) * mm});
            skLineSegment(sketch, "E101", {"start": v(15, 108) * mm, "end": v(33, 90) * mm});
            skLineSegment(sketch, "E102", {"start": v(-80, 0) * mm, "end": v(80, 0) * mm, "construction": true});
            skLineSegment(sketch, "E103.MirrorCS", {"start": v(-15, -108) * mm, "end": v(-15, -120) * mm});
            skLineSegment(sketch, "E104.MirrorCS", {"start": v(15, -120) * mm, "end": v(15, -108) * mm});
            skCircle(sketch, "E105.MirrorC", {"center": v(0, -120) * mm, "radius": 6 * mm});
            skLineSegment(sketch, "E106.MirrorCS", {"start": v(0, -90) * mm, "end": v(0, -120) * mm, "construction": true});
            skArc(sketch, "E107.MirrorCS", {"start": v(-15, -120) * mm, "mid": v(0, -135) * mm, "end": v(15, -120) * mm});
            skLineSegment(sketch, "E108.MirrorCS", {"start": v(-33, -90) * mm, "end": v(-15, -108) * mm});
            skLineSegment(sketch, "E109.MirrorCS", {"start": v(15, -108) * mm, "end": v(33, -90) * mm});
            skSolve(sketch);
        }
        {
            var Q0;
            Q0=makeQuery(id+"F16.imprint","IMPRINT",FACE,{"disambiguationData":[TD([[makeQuery(id+"F16.imprint","IMPRINT",EDGE,{"derivedFrom":sQuery(id+"F16.wireOp",EDGE,"E96")}),-1.0]])]});
            var Q1;
            Q1=makeQuery(id+"F16.imprint","IMPRINT",FACE,{"disambiguationData":[TD([[makeQuery(id+"F16.imprint","IMPRINT",EDGE,{"derivedFrom":sQuery(id+"F16.wireOp",EDGE,"E79.0")}),-1.0]])]});
            var Q2;
            Q2=makeQuery(id+"F16.imprint","IMPRINT",FACE,{"disambiguationData":[TD([[makeQuery(id+"F16.imprint","IMPRINT",EDGE,{"derivedFrom":sQuery(id+"F16.wireOp",EDGE,"E103.MirrorCS")}),1.0]])]});
            var Q3;
            Q3=makeQuery(id+"F2.opExtrude","CAP_FACE",FACE,{"disambiguationData":[OSD([sQuery(id+"F0.wireOp",EDGE,"E12"),sQuery(id+"F0.wireOp",EDGE,"E13"),sQuery(id+"F0.wireOp",EDGE,"E14"),sQuery(id+"F0.wireOp",EDGE,"E15"),sQuery(id+"F0.wireOp",EDGE,"E17.filletArc"),sQuery(id+"F0.wireOp",EDGE,"E18.filletArc"),sQuery(id+"F0.wireOp",EDGE,"E19.filletArc"),sQuery(id+"F0.wireOp",EDGE,"E20.filletArc"),sQuery(id+"F0.wireOp",EDGE,"E25.0"),sQuery(id+"F0.wireOp",EDGE,"E25.1"),sQuery(id+"F0.wireOp",EDGE,"E25.2"),sQuery(id+"F0.wireOp",EDGE,"E25.3"),sQuery(id+"F0.wireOp",EDGE,"E25.4"),sQuery(id+"F0.wireOp",EDGE,"E25.5"),sQuery(id+"F0.wireOp",EDGE,"E25.6"),sQuery(id+"F0.wireOp",EDGE,"E25.7")])],"isStart":false});
            extrude(context, id + "F17", {"entities" : qUnion([Q0, Q1, Q2]), "endBound" : BoundingType.UP_TO_SURFACE, "depth" : 25 * mm, "endBoundEntityFace" : qUnion([Q3]), "offsetDistance" : 25 * mm});
        }
    });
